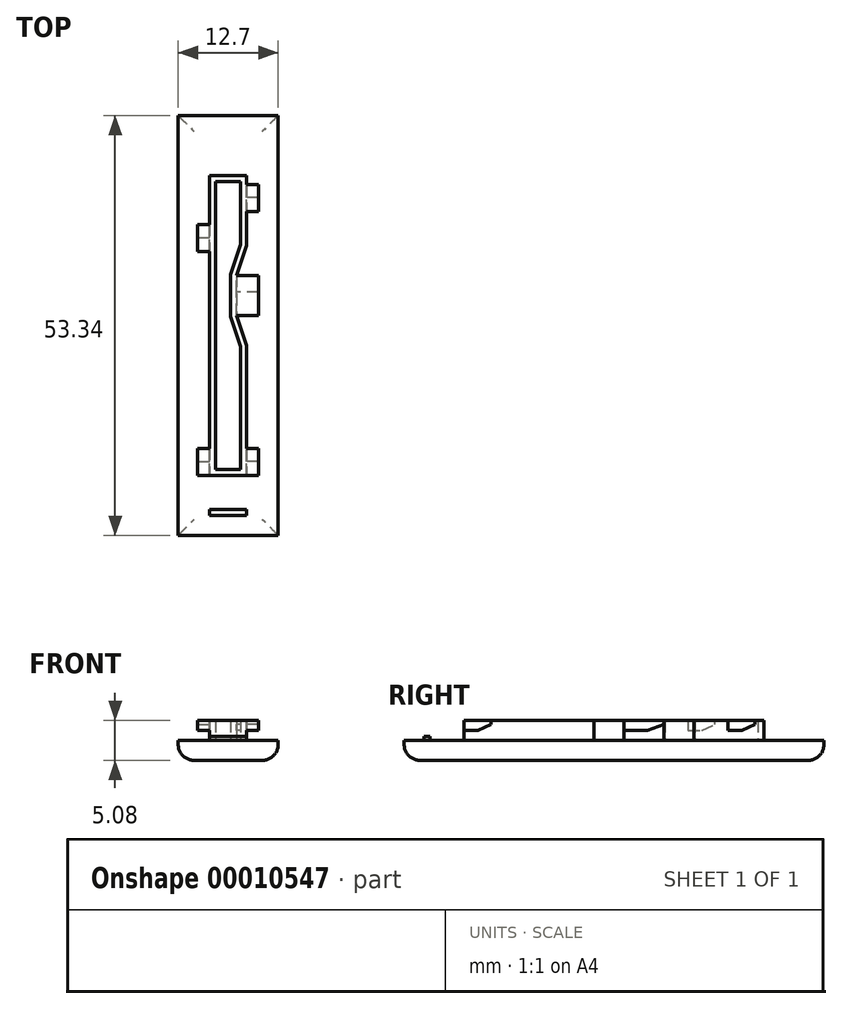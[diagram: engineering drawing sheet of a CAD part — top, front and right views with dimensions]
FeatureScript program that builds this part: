
annotation { "Feature Type Name" : "Feature", "Feature Type Description" : "" }
export const myFeature = defineFeature(function(context is Context, id is Id, definition is map)
    precondition{}
    {
        {
            var Q0;
            Q0=qCreatedBy(makeId("Top.planeOp"),FACE);
            var sketch = newSketch(context, id + "F0", { "sketchPlane" : qUnion([Q0])});
            skLineSegment(sketch, "E0", {"start": v(0, 0) * mm, "end": v(6.35, 0) * mm, "construction": true});
            skLineSegment(sketch, "E1", {"start": v(0, 0) * mm, "end": v(0, 26.67) * mm, "construction": true});
            skLineSegment(sketch, "E2.bottom", {"start": v(-6.35, 26.67) * mm, "end": v(6.35, 26.67) * mm});
            skLineSegment(sketch, "E2.top", {"start": v(-6.35, -26.67) * mm, "end": v(6.35, -26.67) * mm});
            skLineSegment(sketch, "E2.left", {"start": v(-6.35, 26.67) * mm, "end": v(-6.35, -26.67) * mm});
            skLineSegment(sketch, "E2.right", {"start": v(6.35, 26.67) * mm, "end": v(6.35, -26.67) * mm});
            skSolve(sketch);
        }
        {
            var Q0;
            Q0 = qSketchRegion(id + "F0", true);
            extrude(context, id + "F1", {"entities" : qUnion([Q0]), "depth" : 2.54 * mm});
        }
        {
            var Q0;
            Q0=makeQuery(id+"F1.opExtrude","CAP_FACE",FACE,{"disambiguationData":[OSD([sQuery(id+"F0.wireOp",EDGE,"E2.bottom"),sQuery(id+"F0.wireOp",EDGE,"E2.top"),sQuery(id+"F0.wireOp",EDGE,"E2.left"),sQuery(id+"F0.wireOp",EDGE,"E2.right")])],"isStart":false});
            var sketch = newSketch(context, id + "F2", { "sketchPlane" : qUnion([Q0])});
            skLineSegment(sketch, "E3", {"start": v(0, 0) * mm, "end": v(2.35, 0) * mm, "construction": true});
            skLineSegment(sketch, "E4.bottom", {"start": v(-2.35, 19.05) * mm, "end": v(2.35, 19.05) * mm});
            skLineSegment(sketch, "E4.top", {"start": v(-2.35, -19.05) * mm, "end": v(2.35, -19.05) * mm});
            skLineSegment(sketch, "E4.left", {"start": v(-2.35, 19.05) * mm, "end": v(-2.35, -19.05) * mm});
            skLineSegment(sketch, "E4.right", {"start": v(2.35, 19.05) * mm, "end": v(2.35, 10.16) * mm});
            skLineSegment(sketch, "E5", {"start": v(0, 26.67) * mm, "end": v(0, 19.05) * mm, "construction": true});
            skPoint(sketch, "E5.endSnap0", {"position": v(0, 26.67) * mm});
            skLineSegment(sketch, "E6", {"start": v(2.35, 10.16) * mm, "end": v(1.08, 6.35) * mm});
            skLineSegment(sketch, "E7", {"start": v(1.08, 6.35) * mm, "end": v(1.08, 1.27) * mm});
            skLineSegment(sketch, "E8", {"start": v(1.08, 1.27) * mm, "end": v(2.35, -2.54) * mm});
            skLineSegment(sketch, "E9.trimOffspring", {"start": v(2.35, -2.54) * mm, "end": v(2.35, -19.05) * mm});
            skLineSegment(sketch, "E10.0", {"start": v(11.54, 26.67) * mm, "end": v(11.54, -26.67) * mm});
            skLineSegment(sketch, "E11.0", {"start": v(-1.59, 18.29) * mm, "end": v(-1.59, -18.29) * mm});
            skLineSegment(sketch, "E11.1", {"start": v(-1.59, -18.29) * mm, "end": v(1.59, -18.29) * mm});
            skLineSegment(sketch, "E11.2", {"start": v(-1.59, 18.29) * mm, "end": v(1.59, 18.29) * mm});
            skLineSegment(sketch, "E11.3", {"start": v(1.59, -2.66) * mm, "end": v(1.59, -18.29) * mm});
            skLineSegment(sketch, "E11.4", {"start": v(1.59, 18.29) * mm, "end": v(1.59, 10.28) * mm});
            skLineSegment(sketch, "E11.5", {"start": v(1.59, 10.28) * mm, "end": v(0.32, 6.47) * mm});
            skLineSegment(sketch, "E11.6", {"start": v(0.32, 6.47) * mm, "end": v(0.32, 1.15) * mm});
            skLineSegment(sketch, "E11.7", {"start": v(0.32, 1.15) * mm, "end": v(1.59, -2.66) * mm});
            skSolve(sketch);
        }
        {
            var Q0;
            Q0 = qSketchRegion(id + "F2", true);
            extrude(context, id + "F3", {"entities" : qUnion([Q0]), "operationType" : NewBodyOperationType.ADD, "depth" : 2.54 * mm});
        }
        {
            var Q0;
            {var subQ0=sQuery(id+"F0.wireOp",EDGE,"E2.bottom");var subQ1=sQuery(id+"F0.wireOp",EDGE,"E2.left");var subQ2=sQuery(id+"F0.wireOp",EDGE,"E2.top");var subQ3=sQuery(id+"F0.wireOp",EDGE,"E2.right");Q0=makeQuery(id+"F3.boolean.opBoolean","SPLIT",FACE,{"disambiguationData":[TD([makeQuery(id+"F1.opExtrude","SWEPT_FACE",FACE,{"disambiguationData":[OSD([subQ0])]})])],"derivedFrom":makeQuery(id+"F1.opExtrude","CAP_FACE",FACE,{"disambiguationData":[OSD([subQ0,subQ2,subQ1,subQ3])],"isStart":false})});}
            var sketch = newSketch(context, id + "F4", { "sketchPlane" : qUnion([Q0])});
            skLineSegment(sketch, "E12.bottom", {"start": v(-2.35, -23.37) * mm, "end": v(2.35, -23.37) * mm});
            skLineSegment(sketch, "E12.top", {"start": v(-2.35, -24.13) * mm, "end": v(2.35, -24.13) * mm});
            skLineSegment(sketch, "E12.left", {"start": v(-2.35, -23.37) * mm, "end": v(-2.35, -24.13) * mm});
            skLineSegment(sketch, "E12.right", {"start": v(2.35, -23.37) * mm, "end": v(2.35, -24.13) * mm});
            skSolve(sketch);
        }
        {
            var Q0;
            Q0 = qSketchRegion(id + "F4", true);
            extrude(context, id + "F5", {"entities" : qUnion([Q0]), "operationType" : NewBodyOperationType.ADD, "depth" : 0.5 * mm});
        }
        {
            var Q0;
            Q0=makeQuery(id+"F3.opExtrude","SWEPT_FACE",FACE,{"disambiguationData":[OSD([sQuery(id+"F2.wireOp",EDGE,"E4.right")])]});
            var sketch = newSketch(context, id + "F6", { "sketchPlane" : qUnion([Q0])});
            skLineSegment(sketch, "E13", {"start": v(-19.05, 5.08) * mm, "end": v(-19.05, 3.81) * mm});
            skLineSegment(sketch, "E14", {"start": v(-19.05, 3.81) * mm, "end": v(-17.27, 3.81) * mm});
            skLineSegment(sketch, "E15", {"start": v(-17.27, 3.81) * mm, "end": v(-15.62, 4.58) * mm});
            skLineSegment(sketch, "E16", {"start": v(-15.62, 4.58) * mm, "end": v(-15.62, 5.08) * mm});
            skLineSegment(sketch, "E17", {"start": v(-15.62, 5.08) * mm, "end": v(-19.05, 5.08) * mm});
            skLineSegment(sketch, "E18.direction1", {"start": v(-19.05, 3.81) * mm, "end": v(14.48, 3.81) * mm, "construction": true});
            skLineSegment(sketch, "E19.0.1.0", {"start": v(14.48, 5.08) * mm, "end": v(14.48, 3.81) * mm});
            skLineSegment(sketch, "E19.3.1.0", {"start": v(14.48, 3.81) * mm, "end": v(16.26, 3.81) * mm});
            skLineSegment(sketch, "E19.6.1.0", {"start": v(16.26, 3.81) * mm, "end": v(17.9, 4.58) * mm});
            skLineSegment(sketch, "E19.9.1.0", {"start": v(17.9, 5.08) * mm, "end": v(14.48, 5.08) * mm});
            skLineSegment(sketch, "E19.12.1.0", {"start": v(17.9, 4.58) * mm, "end": v(17.9, 5.08) * mm});
            skSolve(sketch);
        }
        {
            var Q0;
            Q0 = qSketchRegion(id + "F6", true);
            extrude(context, id + "F7", {"entities" : qUnion([Q0]), "operationType" : NewBodyOperationType.ADD, "depth" : 1.52 * mm});
        }
        {
            var Q0;
            Q0=makeQuery(id+"F3.opExtrude","SWEPT_FACE",FACE,{"disambiguationData":[OSD([sQuery(id+"F2.wireOp",EDGE,"E4.left")])]});
            var sketch = newSketch(context, id + "F8", { "sketchPlane" : qUnion([Q0])});
            skLineSegment(sketch, "E20.0", {"start": v(15.62, 4.58) * mm, "end": v(15.62, 5.08) * mm});
            skLineSegment(sketch, "E21.0", {"start": v(17.27, 3.81) * mm, "end": v(15.62, 4.58) * mm});
            skLineSegment(sketch, "E22.0", {"start": v(19.05, 3.81) * mm, "end": v(17.27, 3.81) * mm});
            skLineSegment(sketch, "E23.0", {"start": v(15.62, 5.08) * mm, "end": v(19.05, 5.08) * mm});
            skLineSegment(sketch, "E24.0", {"start": v(19.05, 5.08) * mm, "end": v(19.05, 3.81) * mm});
            skPoint(sketch, "E25.orphan", {"position": v(19.05, 2.54) * mm});
            skPoint(sketch, "E26.1.0.0", {"position": v(-9.4, 2.54) * mm});
            skLineSegment(sketch, "E26.1.0.1", {"start": v(-9.4, 5.08) * mm, "end": v(-9.4, 3.81) * mm});
            skLineSegment(sketch, "E26.1.0.2", {"start": v(-12.83, 5.08) * mm, "end": v(-9.4, 5.08) * mm});
            skLineSegment(sketch, "E26.1.0.3", {"start": v(-9.4, 3.81) * mm, "end": v(-11.18, 3.81) * mm});
            skLineSegment(sketch, "E26.1.0.4", {"start": v(-11.18, 3.81) * mm, "end": v(-12.83, 4.58) * mm});
            skLineSegment(sketch, "E26.1.0.5", {"start": v(-12.83, 4.58) * mm, "end": v(-12.83, 5.08) * mm});
            skLineSegment(sketch, "E26.direction1", {"start": v(19.05, 2.54) * mm, "end": v(-9.4, 2.54) * mm, "construction": true});
            skSolve(sketch);
        }
        {
            var Q0;
            Q0 = qSketchRegion(id + "F8", true);
            extrude(context, id + "F9", {"entities" : qUnion([Q0]), "operationType" : NewBodyOperationType.ADD, "depth" : 1.52 * mm});
        }
        {
            var Q0;
            Q0=makeQuery(id+"F3.opExtrude","SWEPT_FACE",FACE,{"disambiguationData":[OSD([sQuery(id+"F2.wireOp",EDGE,"E7")])]});
            var sketch = newSketch(context, id + "F10", { "sketchPlane" : qUnion([Q0])});
            skLineSegment(sketch, "E27", {"start": v(1.27, 5.08) * mm, "end": v(1.27, 3.8) * mm});
            skLineSegment(sketch, "E28", {"start": v(1.27, 3.8) * mm, "end": v(4.23, 3.8) * mm});
            skLineSegment(sketch, "E29", {"start": v(4.23, 3.8) * mm, "end": v(6.35, 4.58) * mm});
            skLineSegment(sketch, "E30", {"start": v(6.35, 4.58) * mm, "end": v(6.35, 5.08) * mm});
            skLineSegment(sketch, "E31", {"start": v(6.35, 5.08) * mm, "end": v(1.27, 5.08) * mm});
            skSolve(sketch);
        }
        {
            var Q0;
            Q0 = qSketchRegion(id + "F10", true);
            var Q1;
            Q1=makeQuery(id+"F7.opExtrude","CAP_FACE",FACE,{"disambiguationData":[OSD([sQuery(id+"F6.wireOp",EDGE,"E19.0.1.0"),sQuery(id+"F6.wireOp",EDGE,"E19.3.1.0"),sQuery(id+"F6.wireOp",EDGE,"E19.6.1.0"),sQuery(id+"F6.wireOp",EDGE,"E19.9.1.0"),sQuery(id+"F6.wireOp",EDGE,"E19.12.1.0")])],"isStart":false});
            extrude(context, id + "F11", {"entities" : qUnion([Q0]), "operationType" : NewBodyOperationType.ADD, "endBound" : BoundingType.UP_TO_SURFACE, "endBoundEntityFace" : qUnion([Q1]), "depth" : 25.4 * mm});
        }
        {
            var Q0;
            Q0=makeQuery(id+"F1.opExtrude","CAP_FACE",FACE,{"disambiguationData":[OSD([sQuery(id+"F0.wireOp",EDGE,"E2.bottom"),sQuery(id+"F0.wireOp",EDGE,"E2.top"),sQuery(id+"F0.wireOp",EDGE,"E2.left"),sQuery(id+"F0.wireOp",EDGE,"E2.right")])],"isStart":true});
            fillet(context, id + "F12", {"entities" : qUnion([Q0]), "radius" : 2.03 * mm, "tangentPropagation" : true, "allowEdgeOverflow" : false});
        }
    });
